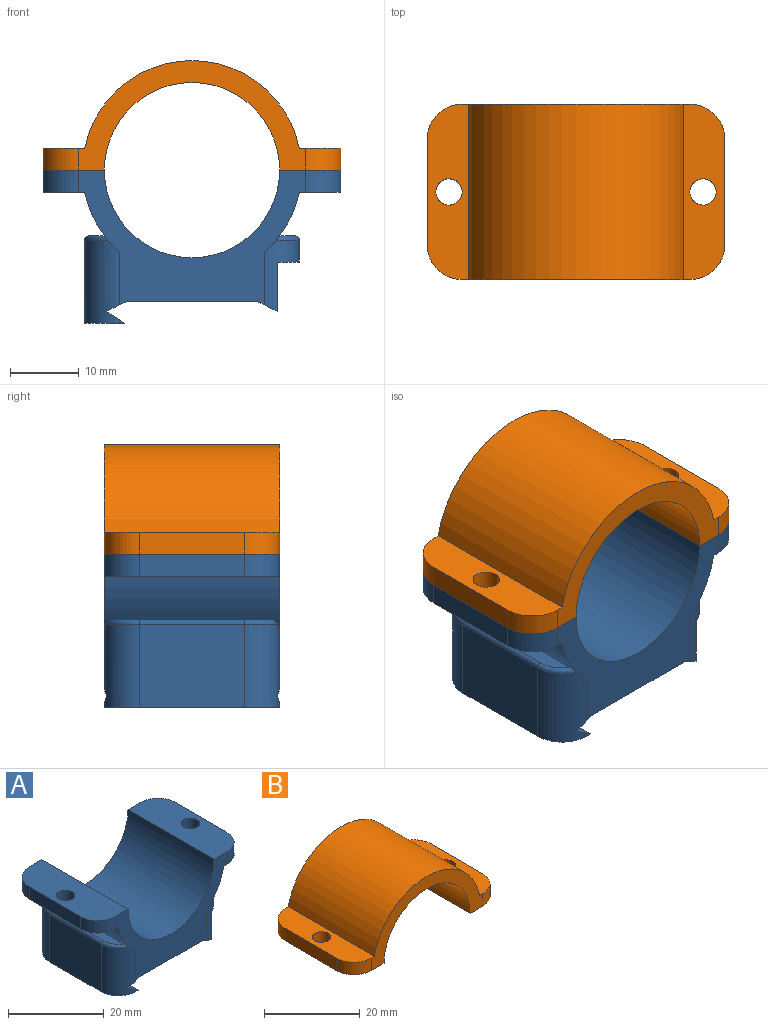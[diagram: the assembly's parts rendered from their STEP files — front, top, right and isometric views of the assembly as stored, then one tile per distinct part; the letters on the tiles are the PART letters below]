
ASSEMBLY  parts=2 mates=1
PART A: 40 faces, bbox 43.2x25.6x22.2 mm
  f0: plane 0.75x0.49mm, normal (0,-1,0), area 0.2mm2, adj f11,f12,f32
  f1: plane 0.75x0.49mm, normal (0,1,0), area 0.2mm2, adj f11,f12,f28
  f2: plane 33.02x19.54mm, normal (0,-1,0), area 240.2mm2, adj f4,f5,f7,f8,f13,f14,f15,f18
  f3: plane 33.02x19.54mm, normal (0,1,0), area 240.2mm2, adj f4,f5,f7,f8,f13,f14,f15,f18
  f4: cylinder r=12.7mm len=25.4mm, axis (0,1,0), area 1013.4mm2, adj f2,f3,f5,f21
  f5: plane 25.4x8.89mm, normal (0,0,1), area 203.3mm2, adj f2,f3,f4,f6,f25,f29,f33
  f6: plane 15.24x3.18mm, normal (-1,0,0), area 48.4mm2, adj f5,f7,f29,f33
  f7: plane 25.4x6.04mm, normal (0,0,-1), area 130.8mm2, adj f2,f3,f6,f8,f25,f29,f33
  f8: cylinder r=15.88mm len=25.4mm, axis (0,1,0), area 179.9mm2, adj f2,f3,f7,f9,f28,f32,f34,f36
  f9: plane 22.94x2.22mm, normal (0,0,1), area 45.9mm2, adj f8,f34,f35,f36
  f10: plane 15.24x12.07mm, normal (-1,0,0), area 183.9mm2, adj f11,f28,f32,f35
  f11: plane 25.4x5.83mm, normal (0,0,-1), area 137.1mm2, adj f0,f1,f10,f12,f28,f32
  f12: plane 25.42x2.68mm, normal (0.55,0,0.84), area 80.1mm2, adj f0,f1,f11,f13,f28,f32
  f13: plane 25.42x2.85mm, normal (0.45,0,-0.89), area 80.1mm2, adj f2,f3,f12,f14,f28,f32
  f14: plane 25.4x19.05mm, normal (0,0,-1), area 483.9mm2, adj f2,f3,f13,f15
  f15: plane 25.42x2.85mm, normal (-0.45,0,-0.89), area 80.2mm2, adj f2,f3,f14,f22,f27,f31
  f16: plane 15.24x3.18mm, normal (1,0,0), area 48.4mm2, adj f23,f27,f31,f38
  f17: plane 22.94x2.22mm, normal (0,0,1), area 45.9mm2, adj f18,f37,f38,f39
  f18: cylinder r=15.88mm len=25.4mm, axis (0,1,0), area 179.9mm2, adj f2,f3,f17,f19,f27,f31,f37,f39
  f19: plane 25.4x6.04mm, normal (0,0,-1), area 130.8mm2, adj f2,f3,f18,f20,f24,f26,f30
  f20: plane 15.24x3.18mm, normal (1,0,0), area 48.4mm2, adj f19,f21,f26,f30
  f21: plane 25.4x8.89mm, normal (0,0,1), area 203.3mm2, adj f2,f3,f4,f20,f24,f26,f30
  f22: plane 24.69x7.15mm, normal (1,0,0), area 176.5mm2, adj f15,f23,f27,f31
  f23: plane 24.69x3.21mm, normal (0,0,-1), area 71mm2, adj f16,f22,f27,f31
  f24: cylinder r=1.91mm len=3.81mm, axis (0,0,-1), area 38mm2, adj f19,f21
  f25: cylinder r=1.91mm len=3.81mm, axis (0,0,-1), area 38mm2, adj f5,f7
  f26: cylinder r=5.08mm len=5.08mm, axis (0,0,1), area 25.3mm2, adj f3,f19,f20,f21
  f27: cylinder r=5.08mm len=10.32mm, axis (0,0,1), area 36.5mm2, adj f3,f15,f16,f18,f22,f23,f37
  f28: cylinder r=5.08mm len=12.07mm, axis (0,0,-1), area 92.6mm2, adj f1,f3,f8,f10,f11,f12,f13,f34
  f29: cylinder r=5.08mm len=5.08mm, axis (0,0,-1), area 25.3mm2, adj f3,f5,f6,f7
  f30: cylinder r=5.08mm len=5.08mm, axis (0,0,-1), area 25.3mm2, adj f2,f19,f20,f21
  f31: cylinder r=5.08mm len=10.32mm, axis (0,0,-1), area 36.5mm2, adj f2,f15,f16,f18,f22,f23,f39
  f32: cylinder r=5.08mm len=12.07mm, axis (0,0,1), area 92.6mm2, adj f0,f2,f8,f10,f11,f12,f13,f36
  f33: cylinder r=5.08mm len=5.08mm, axis (0,0,1), area 25.3mm2, adj f2,f5,f6,f7
  f34: torus R=4.45mm, axis (0,0,1), area 5.5mm2, adj f8,f9,f28,f35
  f35: cylinder r=0.64mm len=15.24mm, axis (0,-1,0), area 15.2mm2, adj f9,f10,f34,f36
  f36: torus R=4.45mm, axis (0,0,1), area 5.5mm2, adj f8,f9,f32,f35
  f37: torus R=4.45mm, axis (0,0,1), area 5.5mm2, adj f17,f18,f27,f38
  f38: cylinder r=0.64mm len=15.24mm, axis (0,1,0), area 15.2mm2, adj f16,f17,f37,f39
  f39: torus R=4.45mm, axis (0,0,1), area 5.5mm2, adj f17,f18,f31,f38
PART B: 16 faces, bbox 43.2x25.4x15.9 mm
  f0: cylinder r=12.7mm len=25.4mm, axis (0,1,0), area 1013.4mm2, adj f1,f7,f8,f9
  f1: plane 25.4x8.89mm, normal (0,0,-1), area 203.3mm2, adj f0,f2,f8,f9,f11,f13,f15
  f2: plane 15.24x3.18mm, normal (1,0,0), area 48.4mm2, adj f1,f3,f13,f15
  f3: plane 25.4x6.04mm, normal (0,0,1), area 130.8mm2, adj f2,f4,f8,f9,f11,f13,f15
  f4: cylinder r=15.88mm len=31.11mm, axis (0,1,0), area 1104.4mm2, adj f3,f5,f8,f9
  f5: plane 25.4x6.04mm, normal (0,0,1), area 130.8mm2, adj f4,f6,f8,f9,f10,f12,f14
  f6: plane 15.24x3.18mm, normal (-1,0,0), area 48.4mm2, adj f5,f7,f12,f14
  f7: plane 25.4x8.89mm, normal (0,0,-1), area 203.3mm2, adj f0,f6,f8,f9,f10,f12,f14
  f8: plane 33.02x15.88mm, normal (0,-1,0), area 147.2mm2, adj f0,f1,f3,f4,f5,f7,f14,f15
  f9: plane 33.02x15.88mm, normal (0,1,0), area 147.2mm2, adj f0,f1,f3,f4,f5,f7,f12,f13
  f10: cylinder r=1.91mm len=3.81mm, axis (0,0,1), area 38mm2, adj f5,f7
  f11: cylinder r=1.91mm len=3.81mm, axis (0,0,1), area 38mm2, adj f1,f3
  f12: cylinder r=5.08mm len=5.08mm, axis (0,0,-1), area 25.3mm2, adj f5,f6,f7,f9
  f13: cylinder r=5.08mm len=5.08mm, axis (0,0,1), area 25.3mm2, adj f1,f2,f3,f9
  f14: cylinder r=5.08mm len=5.08mm, axis (0,0,1), area 25.3mm2, adj f5,f6,f7,f8
  f15: cylinder r=5.08mm len=5.08mm, axis (0,0,-1), area 25.3mm2, adj f1,f2,f3,f8
PLACE A t=(1.78,0.87,10.88)mm fixed
PLACE B t=(1.78,0.87,10.88)mm
MATE planar B.f0 <-> A.f4  axis (0,-1,0) through (1.78,-11.83,10.88)mm
